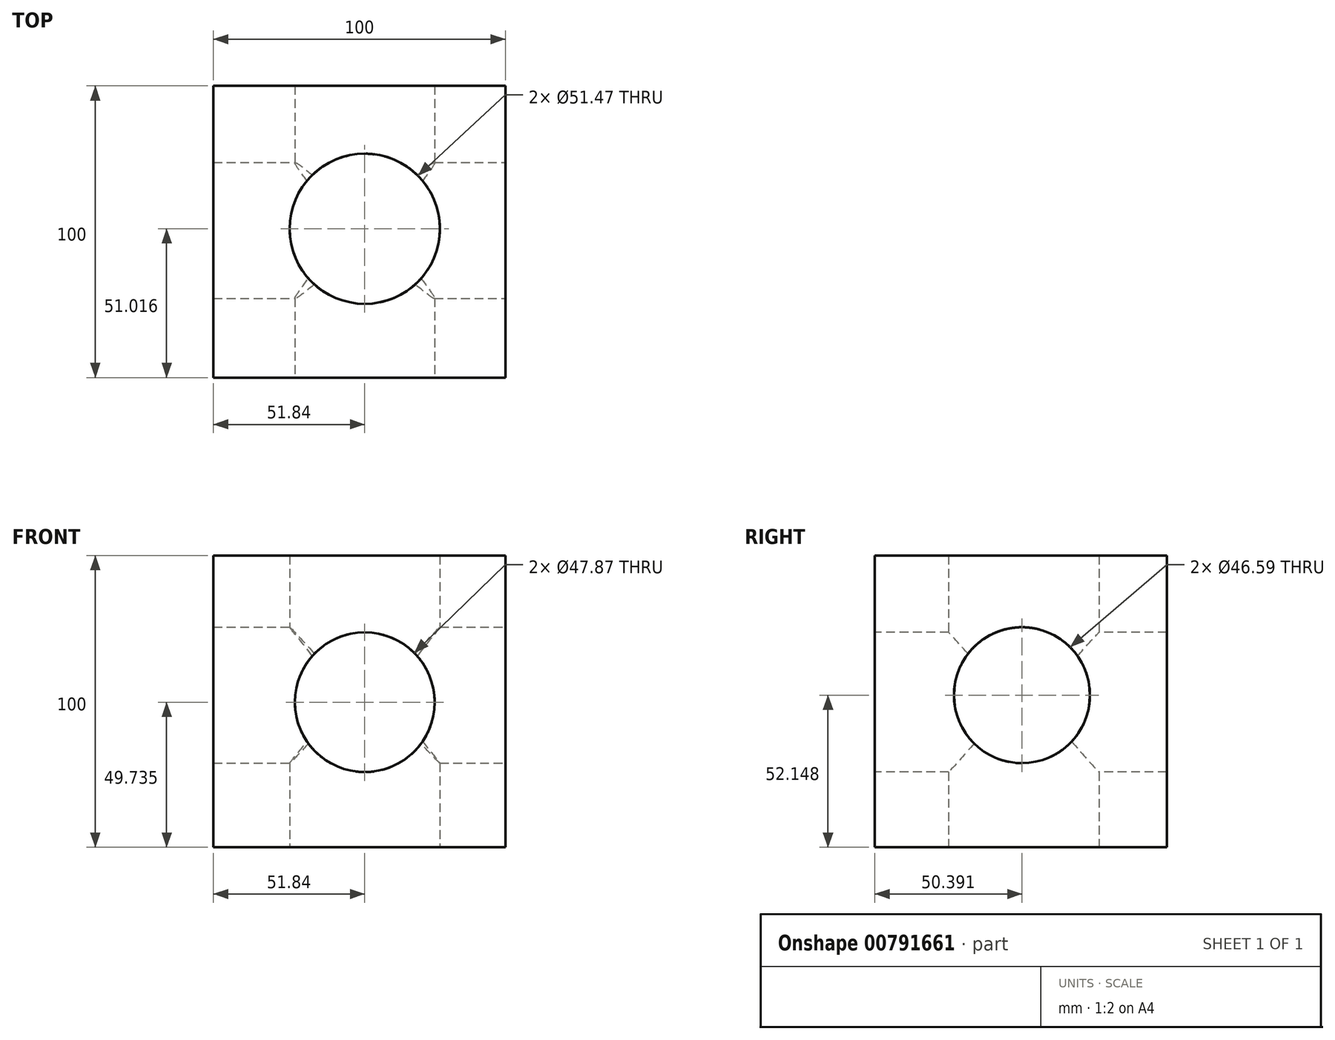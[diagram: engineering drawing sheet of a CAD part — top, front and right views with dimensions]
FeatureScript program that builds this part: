
annotation { "Feature Type Name" : "Feature", "Feature Type Description" : "" }
export const myFeature = defineFeature(function(context is Context, id is Id, definition is map)
    precondition{}
    {
        {
            var Q0;
            Q0=qCreatedBy(makeId("Front.planeOp"),FACE);
            var sketch = newSketch(context, id + "F0", { "sketchPlane" : qUnion([Q0])});
            skLineSegment(sketch, "E0.bottom", {"start": v(-51.84, 58.18) * mm, "end": v(48.16, 58.18) * mm});
            skLineSegment(sketch, "E0.top", {"start": v(-51.84, -41.82) * mm, "end": v(48.16, -41.82) * mm});
            skLineSegment(sketch, "E0.left", {"start": v(-51.84, 58.18) * mm, "end": v(-51.84, -41.82) * mm});
            skLineSegment(sketch, "E0.right", {"start": v(48.16, 58.18) * mm, "end": v(48.16, -41.82) * mm});
            skSolve(sketch);
        }
        {
            var Q0;
            Q0 = qSketchRegion(id + "F0", true);
            extrude(context, id + "F1", {"entities" : qUnion([Q0]), "depth" : 100 * mm, "offsetDistance" : 25 * mm});
        }
        {
            var Q0;
            Q0=makeQuery(id+"F1.opExtrude","SWEPT_FACE",FACE,{"disambiguationData":[OSD([sQuery(id+"F0.wireOp",EDGE,"E0.right")])]});
            var sketch = newSketch(context, id + "F2", { "sketchPlane" : qUnion([Q0])});
            skCircle(sketch, "E1", {"center": v(-49.6, 10.33) * mm, "radius": 23.3 * mm});
            skSolve(sketch);
        }
        {
            var Q0;
            Q0=makeQuery(id+"F2.imprint","IMPRINT",FACE,{"disambiguationData":[TD([[makeQuery(id+"F2.imprint","IMPRINT",EDGE,{"derivedFrom":sQuery(id+"F2.wireOp",EDGE,"E1")}),1.0]])]});
            extrude(context, id + "F3", {"entities" : qUnion([Q0]), "operationType" : NewBodyOperationType.REMOVE, "oppositeDirection" : true, "depth" : 100 * mm, "offsetDistance" : 25 * mm});
        }
        {
            var Q0;
            Q0=makeQuery(id+"F1.opExtrude","SWEPT_FACE",FACE,{"disambiguationData":[OSD([sQuery(id+"F0.wireOp",EDGE,"E0.top")])]});
            var sketch = newSketch(context, id + "F4", { "sketchPlane" : qUnion([Q0])});
            skCircle(sketch, "E2", {"center": v(0, 48.98) * mm, "radius": 25.73 * mm});
            skSolve(sketch);
        }
        {
            var Q0;
            Q0=makeQuery(id+"F4.imprint","IMPRINT",FACE,{"disambiguationData":[TD([[makeQuery(id+"F4.imprint","IMPRINT",EDGE,{"derivedFrom":sQuery(id+"F4.wireOp",EDGE,"E2")}),1.0]])]});
            extrude(context, id + "F5", {"entities" : qUnion([Q0]), "operationType" : NewBodyOperationType.REMOVE, "oppositeDirection" : true, "depth" : 100 * mm, "offsetDistance" : 25 * mm});
        }
        {
            var Q0;
            Q0=makeQuery(id+"F1.opExtrude","CAP_FACE",FACE,{"disambiguationData":[OSD([sQuery(id+"F0.wireOp",EDGE,"E0.bottom"),sQuery(id+"F0.wireOp",EDGE,"E0.top"),sQuery(id+"F0.wireOp",EDGE,"E0.left"),sQuery(id+"F0.wireOp",EDGE,"E0.right")])],"isStart":false});
            var sketch = newSketch(context, id + "F6", { "sketchPlane" : qUnion([Q0])});
            skCircle(sketch, "E3", {"center": v(0, 7.92) * mm, "radius": 23.94 * mm});
            skSolve(sketch);
        }
        {
            var Q0;
            Q0=makeQuery(id+"F6.imprint","IMPRINT",FACE,{"disambiguationData":[TD([[makeQuery(id+"F6.imprint","IMPRINT",EDGE,{"derivedFrom":sQuery(id+"F6.wireOp",EDGE,"E3")}),1.0]])]});
            extrude(context, id + "F7", {"entities" : qUnion([Q0]), "operationType" : NewBodyOperationType.REMOVE, "oppositeDirection" : true, "depth" : 100 * mm, "offsetDistance" : 25 * mm});
        }
    });
